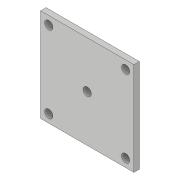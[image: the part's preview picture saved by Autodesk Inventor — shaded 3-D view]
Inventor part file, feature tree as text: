
AUTODESK INVENTOR PART (.ipt)
format: ipt  version: 2019 (Build 230136000, 136)  size: 103,424 bytes
history: native  units: mm
features: extrude x3, sketch x3
ambient origin geometry x8: Origin, YZ Plane, XZ Plane, XY Plane, X Axis, Y Axis, Z Axis, Center Point
bodies: Solid1 (feature_tree)
feature tree (6):
  extrude  "Extrusion1"  Depth=170.0mm
  extrude  "Extrusion2"  Depth=10.0mm
  extrude  "Extrusion3"  Depth=10.0mm
  sketch  "Sketch1"  dims[d0=170.0mm d1=170.0mm]
  sketch  "Sketch2"  dims[d2=10.0mm d3=0.0mm d4=15.0mm]
  sketch  "Sketch3"  dims[d5=15.0mm d6=155.0mm d7=140.0mm d8=140.0mm d9=140.0mm d10=15.0mm d11=15.0mm d12=15.0mm d13=15.0mm d14=10.0mm d15=0.0mm d16=85.0mm d17=85.0mm d18=15.0mm d19=10.0mm d20=0.0mm]
